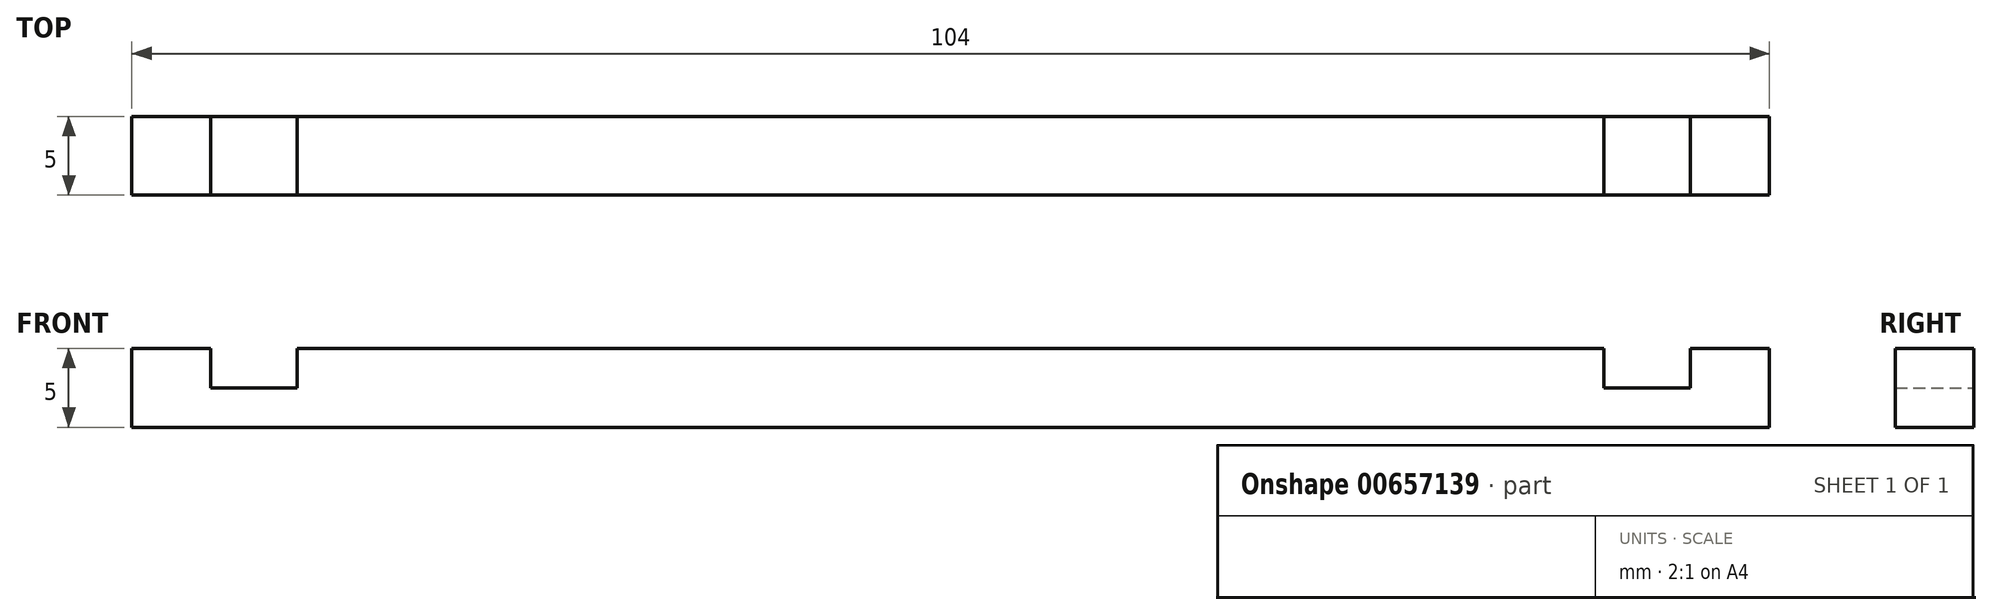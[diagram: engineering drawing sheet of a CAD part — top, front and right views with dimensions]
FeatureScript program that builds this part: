
annotation { "Feature Type Name" : "Feature", "Feature Type Description" : "" }
export const myFeature = defineFeature(function(context is Context, id is Id, definition is map)
    precondition{}
    {
        {
            var Q0;
            Q0=qCreatedBy(makeId("Front.planeOp"),FACE);
            var sketch = newSketch(context, id + "F0", { "sketchPlane" : qUnion([Q0])});
            skLineSegment(sketch, "E0", {"start": v(-52, 0) * mm, "end": v(52, 0) * mm});
            skLineSegment(sketch, "E1", {"start": v(52, 0) * mm, "end": v(52, 5) * mm});
            skLineSegment(sketch, "E2", {"start": v(52, 5) * mm, "end": v(47, 5) * mm});
            skLineSegment(sketch, "E3", {"start": v(-52, 5) * mm, "end": v(-52, 0) * mm});
            skLineSegment(sketch, "E4", {"start": v(-47, 5) * mm, "end": v(-47, 2.5) * mm});
            skLineSegment(sketch, "E5", {"start": v(-47, 2.5) * mm, "end": v(-41.5, 2.5) * mm});
            skLineSegment(sketch, "E6", {"start": v(-41.5, 2.5) * mm, "end": v(-41.5, 5) * mm});
            skLineSegment(sketch, "E7.trimOffspring", {"start": v(-47, 5) * mm, "end": v(-52, 5) * mm});
            skLineSegment(sketch, "E8.MirrorCS", {"start": v(47, 2.5) * mm, "end": v(41.5, 2.5) * mm});
            skLineSegment(sketch, "E9.MirrorCS", {"start": v(47, 5) * mm, "end": v(47, 2.5) * mm});
            skLineSegment(sketch, "E10.MirrorCS", {"start": v(41.5, 2.5) * mm, "end": v(41.5, 5) * mm});
            skLineSegment(sketch, "E11.trimOffspring", {"start": v(41.5, 5) * mm, "end": v(-41.5, 5) * mm});
            skSolve(sketch);
        }
        {
            var Q0;
            Q0=makeQuery(id+"F0.imprint","IMPRINT",FACE,{"disambiguationData":[TD([[makeQuery(id+"F0.imprint","IMPRINT",EDGE,{"derivedFrom":sQuery(id+"F0.wireOp",EDGE,"E0")}),1.0]])]});
            extrude(context, id + "F1", {"entities" : qUnion([Q0]), "depth" : 5 * mm, "offsetDistance" : 25 * mm});
        }
    });
